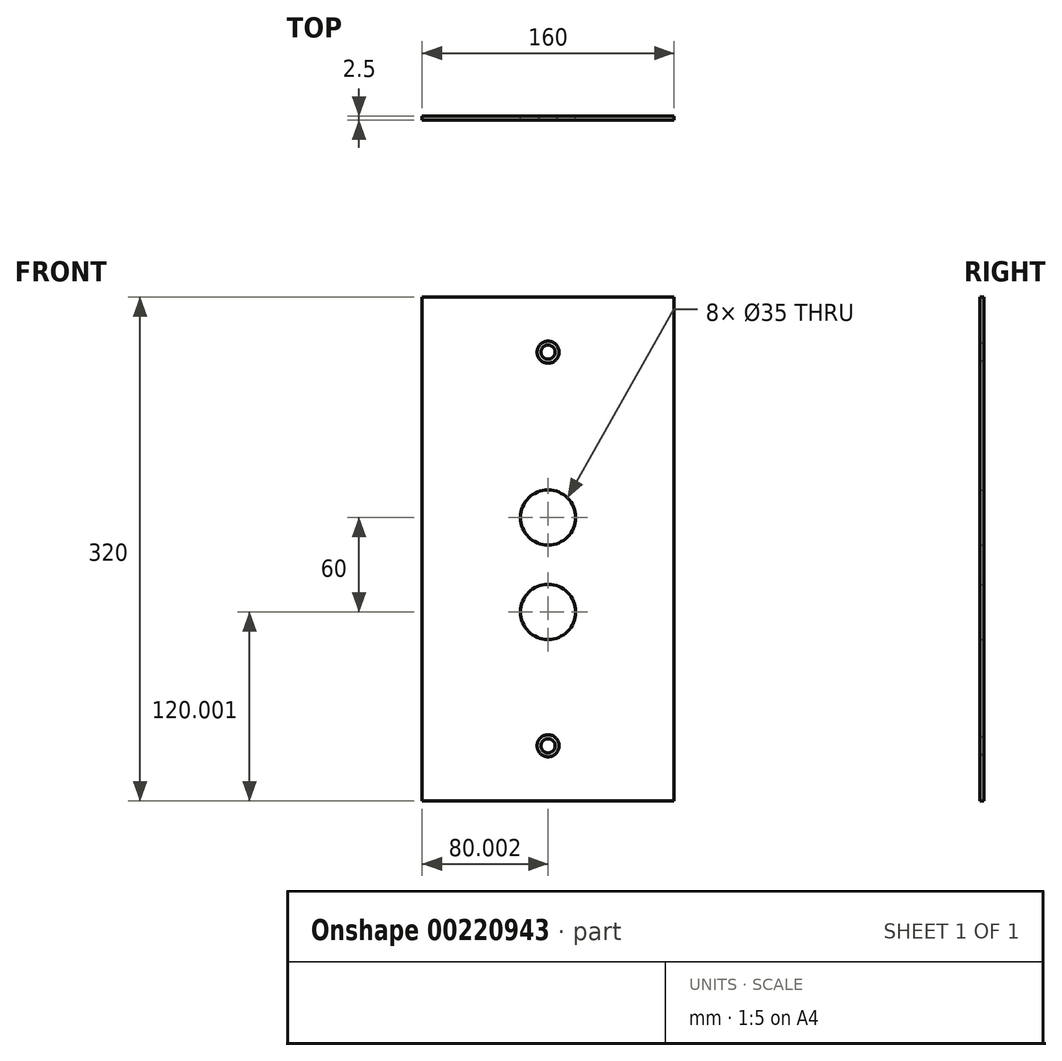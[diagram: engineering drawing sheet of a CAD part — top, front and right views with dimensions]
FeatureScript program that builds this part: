
annotation { "Feature Type Name" : "Feature", "Feature Type Description" : "" }
export const myFeature = defineFeature(function(context is Context, id is Id, definition is map)
    precondition{}
    {
        {
            var Q0;
            Q0=qCreatedBy(makeId("Front.planeOp"),FACE);
            var sketch = newSketch(context, id + "F0", { "sketchPlane" : qUnion([Q0])});
            skLineSegment(sketch, "E0.bottom", {"start": v(-81.89, 189.68) * mm, "end": v(78.11, 189.68) * mm});
            skLineSegment(sketch, "E0.top", {"start": v(-81.89, -130.32) * mm, "end": v(78.11, -130.32) * mm});
            skLineSegment(sketch, "E0.left", {"start": v(-81.89, 189.68) * mm, "end": v(-81.89, -130.32) * mm});
            skLineSegment(sketch, "E0.right", {"start": v(78.11, 189.68) * mm, "end": v(78.11, -130.32) * mm});
            skLineSegment(sketch, "E1", {"start": v(-1.89, 189.68) * mm, "end": v(-1.89, -130.32) * mm, "construction": true});
            skCircle(sketch, "E2", {"center": v(-1.89, 154.68) * mm, "radius": 3 * mm});
            skCircle(sketch, "E3", {"center": v(-1.89, -95.32) * mm, "radius": 3 * mm});
            skCircle(sketch, "E4", {"center": v(-1.89, -10.32) * mm, "radius": 17.5 * mm});
            skCircle(sketch, "E5", {"center": v(-1.89, 49.68) * mm, "radius": 17.5 * mm});
            skSolve(sketch);
        }
        {
            var Q0;
            Q0=makeQuery(id+"F0.imprint","IMPRINT",FACE,{"disambiguationData":[TD([[makeQuery(id+"F0.imprint","IMPRINT",EDGE,{"derivedFrom":sQuery(id+"F0.wireOp",EDGE,"E0.bottom")}),-1.0]])]});
            extrude(context, id + "F1", {"entities" : qUnion([Q0]), "depth" : 2.5 * mm});
        }
        {
            var Q0;
            Q0=makeQuery(id+"F1.opExtrude","CAP_EDGE",EDGE,{"disambiguationData":[OSD([sQuery(id+"F0.wireOp",EDGE,"E2")])],"isStart":false});
            var Q1;
            Q1=makeQuery(id+"F1.opExtrude","CAP_EDGE",EDGE,{"disambiguationData":[OSD([sQuery(id+"F0.wireOp",EDGE,"E3")])],"isStart":false});
            chamfer(context, id + "F2", {"entities" : qUnion([Q0, Q1]), "chamferType" : ChamferType.OFFSET_ANGLE, "width" : 4 * mm, "oppositeDirection" : false, "angle" : 45 * degree, "tangentPropagation" : true});
        }
    });
